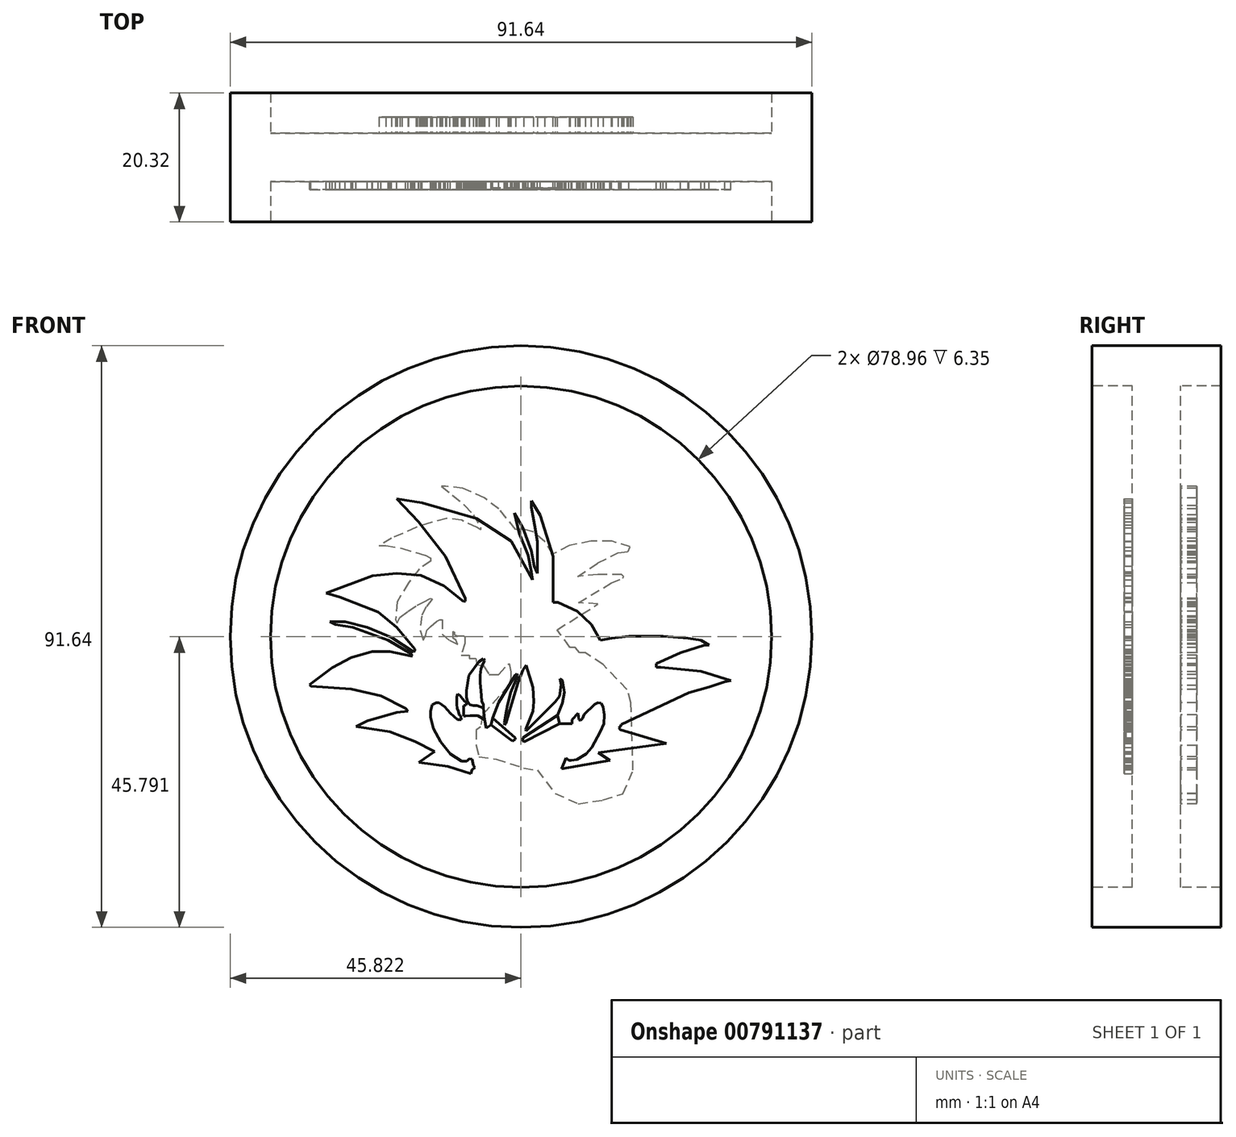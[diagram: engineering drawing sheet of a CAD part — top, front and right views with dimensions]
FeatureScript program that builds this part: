
annotation { "Feature Type Name" : "Feature", "Feature Type Description" : "" }
export const myFeature = defineFeature(function(context is Context, id is Id, definition is map)
    precondition{}
    {
        {
            var Q0;
            Q0=qCreatedBy(makeId("Front.planeOp"),FACE);
            var sketch = newSketch(context, id + "F0", { "sketchPlane" : qUnion([Q0])});
            skLineSegment(sketch, "E0", {"start": v(6.69, 2.2) * mm, "end": v(14.29, 3.57) * mm});
            skLineSegment(sketch, "E1", {"start": v(14.29, 3.57) * mm, "end": v(12.43, 4.77) * mm});
            skLineSegment(sketch, "E2", {"start": v(12.43, 4.77) * mm, "end": v(23.14, 6.2) * mm});
            skLineSegment(sketch, "E3", {"start": v(23.14, 6.2) * mm, "end": v(15.9, 8.36) * mm});
            skLineSegment(sketch, "E4", {"start": v(33.33, 16.13) * mm, "end": v(28.65, 17.57) * mm});
            skLineSegment(sketch, "E5", {"start": v(28.65, 17.57) * mm, "end": v(22.24, 18.23) * mm});
            skLineSegment(sketch, "E6", {"start": v(22.24, 18.23) * mm, "end": v(21.59, 18.23) * mm});
            skLineSegment(sketch, "E7", {"start": v(21.59, 18.23) * mm, "end": v(21.59, 18.77) * mm});
            skLineSegment(sketch, "E8", {"start": v(21.59, 18.77) * mm, "end": v(25.36, 20.5) * mm});
            skLineSegment(sketch, "E9", {"start": v(25.36, 20.5) * mm, "end": v(29.19, 21.7) * mm});
            skLineSegment(sketch, "E10", {"start": v(29.19, 21.7) * mm, "end": v(29.88, 21.7) * mm});
            skLineSegment(sketch, "E11", {"start": v(29.88, 21.7) * mm, "end": v(28.64, 22.43) * mm});
            skLineSegment(sketch, "E12", {"start": v(28.64, 22.43) * mm, "end": v(26.6, 22.76) * mm});
            skLineSegment(sketch, "E13", {"start": v(26.6, 22.76) * mm, "end": v(22.63, 23.11) * mm});
            skLineSegment(sketch, "E14", {"start": v(22.63, 23.11) * mm, "end": v(17.27, 23.11) * mm});
            skLineSegment(sketch, "E15", {"start": v(17.27, 23.11) * mm, "end": v(14.56, 22.79) * mm});
            skLineSegment(sketch, "E16", {"start": v(14.56, 22.79) * mm, "end": v(12.77, 22.49) * mm});
            skLineSegment(sketch, "E17", {"start": v(12.77, 22.49) * mm, "end": v(11.34, 24.94) * mm});
            skLineSegment(sketch, "E18", {"start": v(11.34, 24.94) * mm, "end": v(9.16, 27.06) * mm});
            skLineSegment(sketch, "E19", {"start": v(9.16, 27.06) * mm, "end": v(6.07, 28.46) * mm});
            skLineSegment(sketch, "E20", {"start": v(6.07, 28.46) * mm, "end": v(5.34, 28.46) * mm});
            skLineSegment(sketch, "E21", {"start": v(5.34, 28.46) * mm, "end": v(5.34, 35.65) * mm});
            skLineSegment(sketch, "E22", {"start": v(5.34, 35.65) * mm, "end": v(4.38, 38.73) * mm});
            skLineSegment(sketch, "E23", {"start": v(4.38, 38.73) * mm, "end": v(3.32, 42.13) * mm});
            skLineSegment(sketch, "E24", {"start": v(3.32, 42.13) * mm, "end": v(1.92, 44.45) * mm});
            skLineSegment(sketch, "E25", {"start": v(1.92, 44.45) * mm, "end": v(1.92, 43.43) * mm});
            skLineSegment(sketch, "E26", {"start": v(1.92, 43.43) * mm, "end": v(2.4, 40.62) * mm});
            skLineSegment(sketch, "E27", {"start": v(2.4, 40.62) * mm, "end": v(2.87, 38.04) * mm});
            skLineSegment(sketch, "E28", {"start": v(2.87, 38.04) * mm, "end": v(2.87, 33.02) * mm});
            skLineSegment(sketch, "E29", {"start": v(2.87, 33.02) * mm, "end": v(2.34, 34.15) * mm});
            skLineSegment(sketch, "E30", {"start": v(2.34, 34.15) * mm, "end": v(1.92, 36.55) * mm});
            skLineSegment(sketch, "E31", {"start": v(1.92, 36.55) * mm, "end": v(0.54, 40.2) * mm});
            skLineSegment(sketch, "E32", {"start": v(0.54, 40.2) * mm, "end": v(-0.78, 42.53) * mm});
            skLineSegment(sketch, "E33", {"start": v(-0.78, 42.53) * mm, "end": v(0, 39.3) * mm});
            skLineSegment(sketch, "E34", {"start": v(0, 39.3) * mm, "end": v(0.9, 37.15) * mm});
            skLineSegment(sketch, "E35", {"start": v(0.9, 37.15) * mm, "end": v(1.4, 35.88) * mm});
            skLineSegment(sketch, "E36", {"start": v(1.4, 35.88) * mm, "end": v(1.92, 33.27) * mm});
            skLineSegment(sketch, "E37", {"start": v(1.92, 33.27) * mm, "end": v(2.05, 31.99) * mm});
            skLineSegment(sketch, "E38", {"start": v(2.05, 31.99) * mm, "end": v(-1.3, 38.06) * mm});
            skLineSegment(sketch, "E39", {"start": v(-1.3, 38.06) * mm, "end": v(-6.74, 41.63) * mm});
            skLineSegment(sketch, "E40", {"start": v(-6.74, 41.63) * mm, "end": v(-15.3, 44.12) * mm});
            skLineSegment(sketch, "E41", {"start": v(-15.3, 44.12) * mm, "end": v(-19.32, 44.78) * mm});
            skLineSegment(sketch, "E42", {"start": v(-19.32, 44.78) * mm, "end": v(-15.9, 41.15) * mm});
            skLineSegment(sketch, "E43", {"start": v(-15.9, 41.15) * mm, "end": v(-11.62, 35.7) * mm});
            skLineSegment(sketch, "E44", {"start": v(-11.62, 35.7) * mm, "end": v(-8.53, 29.1) * mm});
            skLineSegment(sketch, "E45", {"start": v(-8.53, 29.1) * mm, "end": v(-8.53, 28.6) * mm});
            skLineSegment(sketch, "E46", {"start": v(-8.53, 28.6) * mm, "end": v(-8.77, 28.58) * mm});
            skLineSegment(sketch, "E47", {"start": v(-8.77, 28.58) * mm, "end": v(-11.9, 31.02) * mm});
            skLineSegment(sketch, "E48", {"start": v(-11.9, 31.02) * mm, "end": v(-15.5, 32.67) * mm});
            skLineSegment(sketch, "E49", {"start": v(-15.5, 32.67) * mm, "end": v(-19.32, 33.02) * mm});
            skLineSegment(sketch, "E50", {"start": v(-19.32, 33.02) * mm, "end": v(-23.1, 32.62) * mm});
            skLineSegment(sketch, "E51", {"start": v(-23.1, 32.62) * mm, "end": v(-30.42, 29.92) * mm});
            skLineSegment(sketch, "E52", {"start": v(-30.42, 29.92) * mm, "end": v(-28.29, 29.28) * mm});
            skLineSegment(sketch, "E53", {"start": v(-28.29, 29.28) * mm, "end": v(-22.24, 26.94) * mm});
            skLineSegment(sketch, "E54", {"start": v(-22.24, 26.94) * mm, "end": v(-19.32, 24.52) * mm});
            skLineSegment(sketch, "E55", {"start": v(-19.32, 24.52) * mm, "end": v(-16.47, 21.1) * mm});
            skLineSegment(sketch, "E56", {"start": v(-16.47, 21.1) * mm, "end": v(-16.47, 20.78) * mm});
            skLineSegment(sketch, "E57", {"start": v(-16.47, 20.78) * mm, "end": v(-16.65, 20.64) * mm});
            skLineSegment(sketch, "E58", {"start": v(-16.65, 20.64) * mm, "end": v(-20.12, 22.92) * mm});
            skLineSegment(sketch, "E59", {"start": v(-20.12, 22.92) * mm, "end": v(-23.94, 24.52) * mm});
            skLineSegment(sketch, "E60", {"start": v(-23.94, 24.52) * mm, "end": v(-27.47, 25.39) * mm});
            skLineSegment(sketch, "E61", {"start": v(-27.47, 25.39) * mm, "end": v(-29.83, 25.39) * mm});
            skLineSegment(sketch, "E62", {"start": v(-29.83, 25.39) * mm, "end": v(-29, 24.92) * mm});
            skLineSegment(sketch, "E63", {"start": v(-29, 24.92) * mm, "end": v(-26.27, 24.52) * mm});
            skLineSegment(sketch, "E64", {"start": v(-26.27, 24.52) * mm, "end": v(-20.64, 22.5) * mm});
            skLineSegment(sketch, "E65", {"start": v(-20.64, 22.5) * mm, "end": v(-17.1, 20.37) * mm});
            skLineSegment(sketch, "E66", {"start": v(-17.1, 20.37) * mm, "end": v(-16.81, 20.02) * mm});
            skLineSegment(sketch, "E67", {"start": v(-16.81, 20.02) * mm, "end": v(-17.1, 20.02) * mm});
            skLineSegment(sketch, "E68", {"start": v(-17.1, 20.02) * mm, "end": v(-20.39, 20.71) * mm});
            skLineSegment(sketch, "E69", {"start": v(-20.39, 20.71) * mm, "end": v(-23.2, 20.71) * mm});
            skLineSegment(sketch, "E70", {"start": v(-23.2, 20.71) * mm, "end": v(-26.48, 19.74) * mm});
            skLineSegment(sketch, "E71", {"start": v(-26.48, 19.74) * mm, "end": v(-29.49, 18.17) * mm});
            skLineSegment(sketch, "E72", {"start": v(-29.49, 18.17) * mm, "end": v(-33.04, 15.49) * mm});
            skLineSegment(sketch, "E73", {"start": v(-33.04, 15.49) * mm, "end": v(-32.85, 15.23) * mm});
            skLineSegment(sketch, "E74", {"start": v(-32.85, 15.23) * mm, "end": v(-26.48, 14.77) * mm});
            skLineSegment(sketch, "E75", {"start": v(-26.48, 14.77) * mm, "end": v(-21.8, 13.7) * mm});
            skLineSegment(sketch, "E76", {"start": v(-21.8, 13.7) * mm, "end": v(-17.92, 11.75) * mm});
            skLineSegment(sketch, "E77", {"start": v(-17.92, 11.75) * mm, "end": v(-17.56, 11.31) * mm});
            skLineSegment(sketch, "E78", {"start": v(-17.56, 11.31) * mm, "end": v(-19.32, 11.13) * mm});
            skLineSegment(sketch, "E79", {"start": v(-19.32, 11.13) * mm, "end": v(-23.93, 9.75) * mm});
            skLineSegment(sketch, "E80", {"start": v(-23.93, 9.75) * mm, "end": v(-25.75, 8.87) * mm});
            skLineSegment(sketch, "E81", {"start": v(-25.75, 8.87) * mm, "end": v(-20.4, 8.05) * mm});
            skLineSegment(sketch, "E82", {"start": v(-20.4, 8.05) * mm, "end": v(-16.47, 6.52) * mm});
            skLineSegment(sketch, "E83", {"start": v(-16.47, 6.52) * mm, "end": v(-13.33, 4.92) * mm});
            skLineSegment(sketch, "E84", {"start": v(-13.33, 4.92) * mm, "end": v(-15.85, 3.22) * mm});
            skLineSegment(sketch, "E85", {"start": v(-15.85, 3.22) * mm, "end": v(-11.27, 2.57) * mm});
            skLineSegment(sketch, "E86", {"start": v(-11.27, 2.57) * mm, "end": v(-7.62, 1.43) * mm});
            skLineSegment(sketch, "E87", {"start": v(-7.62, 1.43) * mm, "end": v(-7.42, 2.08) * mm});
            skLineSegment(sketch, "E88", {"start": v(-7.42, 2.08) * mm, "end": v(-6.99, 2.42) * mm});
            skLineSegment(sketch, "E89", {"start": v(-6.99, 2.42) * mm, "end": v(-7.26, 2.76) * mm});
            skLineSegment(sketch, "E90", {"start": v(-7.26, 2.76) * mm, "end": v(-7.45, 3.76) * mm});
            skLineSegment(sketch, "E91", {"start": v(-7.45, 3.76) * mm, "end": v(-7.87, 3.79) * mm});
            skLineSegment(sketch, "E92", {"start": v(-7.87, 3.79) * mm, "end": v(-8.25, 3.39) * mm});
            skLineSegment(sketch, "E93", {"start": v(-8.25, 3.39) * mm, "end": v(-9.1, 3.45) * mm});
            skLineSegment(sketch, "E94", {"start": v(-9.1, 3.45) * mm, "end": v(-10.85, 4.56) * mm});
            skLineSegment(sketch, "E95", {"start": v(-10.85, 4.56) * mm, "end": v(-12.41, 6.46) * mm});
            skLineSegment(sketch, "E96", {"start": v(-12.41, 6.46) * mm, "end": v(-13.57, 8.58) * mm});
            skLineSegment(sketch, "E97", {"start": v(-13.57, 8.58) * mm, "end": v(-14.01, 10.34) * mm});
            skLineSegment(sketch, "E98", {"start": v(-14.01, 10.34) * mm, "end": v(-14.01, 11.32) * mm});
            skLineSegment(sketch, "E99", {"start": v(-14.01, 11.32) * mm, "end": v(-13.71, 12.28) * mm});
            skLineSegment(sketch, "E100", {"start": v(-13.71, 12.28) * mm, "end": v(-13.07, 12.65) * mm});
            skLineSegment(sketch, "E101", {"start": v(-13.07, 12.65) * mm, "end": v(-12.65, 12.62) * mm});
            skLineSegment(sketch, "E102", {"start": v(-12.65, 12.62) * mm, "end": v(-11.74, 11.98) * mm});
            skLineSegment(sketch, "E103", {"start": v(-11.74, 11.98) * mm, "end": v(-10.88, 10.95) * mm});
            skLineSegment(sketch, "E104", {"start": v(-10.88, 10.95) * mm, "end": v(-9.74, 9.99) * mm});
            skLineSegment(sketch, "E105", {"start": v(-9.74, 9.99) * mm, "end": v(-9.17, 9.94) * mm});
            skLineSegment(sketch, "E106", {"start": v(-9.17, 9.94) * mm, "end": v(-9.23, 10.5) * mm});
            skLineSegment(sketch, "E107", {"start": v(-9.23, 10.5) * mm, "end": v(-9.48, 10.72) * mm});
            skLineSegment(sketch, "E108", {"start": v(-9.48, 10.72) * mm, "end": v(-9.58, 11.26) * mm});
            skLineSegment(sketch, "E109", {"start": v(-9.58, 11.26) * mm, "end": v(-9.77, 11.77) * mm});
            skLineSegment(sketch, "E110", {"start": v(-9.77, 11.77) * mm, "end": v(-9.87, 12.38) * mm});
            skLineSegment(sketch, "E111", {"start": v(-9.87, 12.38) * mm, "end": v(-9.87, 13.54) * mm});
            skLineSegment(sketch, "E112", {"start": v(-9.87, 13.54) * mm, "end": v(-9.74, 14.03) * mm});
            skLineSegment(sketch, "E113", {"start": v(-9.74, 14.03) * mm, "end": v(-9.38, 13.8) * mm});
            skLineSegment(sketch, "E114", {"start": v(-9.38, 13.8) * mm, "end": v(-8.94, 13.27) * mm});
            skLineSegment(sketch, "E115", {"start": v(-8.94, 13.27) * mm, "end": v(-8.56, 12.8) * mm});
            skLineSegment(sketch, "E116", {"start": v(-8.56, 12.8) * mm, "end": v(-8.38, 12.7) * mm});
            skLineSegment(sketch, "E117", {"start": v(-8.38, 12.7) * mm, "end": v(-8.35, 12.54) * mm});
            skLineSegment(sketch, "E118", {"start": v(-8.35, 12.54) * mm, "end": v(-8.38, 12.22) * mm});
            skLineSegment(sketch, "E119", {"start": v(-8.38, 12.22) * mm, "end": v(-8.78, 12.15) * mm});
            skLineSegment(sketch, "E120", {"start": v(-8.78, 12.15) * mm, "end": v(-8.78, 10.53) * mm});
            skLineSegment(sketch, "E121", {"start": v(-8.78, 10.53) * mm, "end": v(-8.43, 10.5) * mm});
            skLineSegment(sketch, "E122", {"start": v(-8.43, 10.5) * mm, "end": v(-7.78, 10.61) * mm});
            skLineSegment(sketch, "E123", {"start": v(-7.78, 10.61) * mm, "end": v(-7.1, 10.61) * mm});
            skLineSegment(sketch, "E124", {"start": v(-7.1, 10.61) * mm, "end": v(-6.58, 10.58) * mm});
            skLineSegment(sketch, "E125", {"start": v(-6.58, 10.58) * mm, "end": v(-5.45, 9.94) * mm});
            skLineSegment(sketch, "E126", {"start": v(-5.45, 9.94) * mm, "end": v(-5.23, 8.63) * mm});
            skLineSegment(sketch, "E127", {"start": v(-5.23, 8.63) * mm, "end": v(-4.43, 9.13) * mm});
            skLineSegment(sketch, "E128", {"start": v(-4.43, 9.13) * mm, "end": v(-1.1, 6.6) * mm});
            skLineSegment(sketch, "E129", {"start": v(-1.1, 6.6) * mm, "end": v(-0.65, 6.83) * mm});
            skLineSegment(sketch, "E130", {"start": v(-0.65, 6.83) * mm, "end": v(-0.65, 7.12) * mm});
            skLineSegment(sketch, "E131", {"start": v(-0.65, 7.12) * mm, "end": v(-2.15, 8.44) * mm});
            skLineSegment(sketch, "E132", {"start": v(-2.15, 8.44) * mm, "end": v(-4.2, 10.24) * mm});
            skLineSegment(sketch, "E133", {"start": v(-4.2, 10.24) * mm, "end": v(-3.22, 12.7) * mm});
            skLineSegment(sketch, "E134", {"start": v(-3.22, 12.7) * mm, "end": v(-0.65, 16.91) * mm});
            skLineSegment(sketch, "E135", {"start": v(-0.65, 16.91) * mm, "end": v(-0.42, 17.16) * mm});
            skLineSegment(sketch, "E136", {"start": v(-0.42, 17.16) * mm, "end": v(-0.27, 16.9) * mm});
            skLineSegment(sketch, "E137", {"start": v(-0.27, 16.9) * mm, "end": v(-1.36, 14.26) * mm});
            skLineSegment(sketch, "E138", {"start": v(-1.36, 14.26) * mm, "end": v(-1.85, 12.28) * mm});
            skLineSegment(sketch, "E139", {"start": v(-1.85, 12.28) * mm, "end": v(-2.07, 11.26) * mm});
            skLineSegment(sketch, "E140", {"start": v(-2.07, 11.26) * mm, "end": v(-2.35, 9.44) * mm});
            skLineSegment(sketch, "E141", {"start": v(-2.35, 9.44) * mm, "end": v(-2.3, 9.1) * mm});
            skLineSegment(sketch, "E142", {"start": v(-2.3, 9.1) * mm, "end": v(-2.08, 9.39) * mm});
            skLineSegment(sketch, "E143", {"start": v(-2.08, 9.39) * mm, "end": v(-1.23, 12.41) * mm});
            skLineSegment(sketch, "E144", {"start": v(-1.23, 12.41) * mm, "end": v(-0.23, 15.78) * mm});
            skLineSegment(sketch, "E145", {"start": v(-0.23, 15.78) * mm, "end": v(0.58, 17.74) * mm});
            skLineSegment(sketch, "E146", {"start": v(0.58, 17.74) * mm, "end": v(1.04, 18.55) * mm});
            skLineSegment(sketch, "E147", {"start": v(1.04, 18.55) * mm, "end": v(2.14, 15.06) * mm});
            skLineSegment(sketch, "E148", {"start": v(2.14, 15.06) * mm, "end": v(2.29, 12.82) * mm});
            skLineSegment(sketch, "E149", {"start": v(2.29, 12.82) * mm, "end": v(2.18, 11.26) * mm});
            skLineSegment(sketch, "E150", {"start": v(2.18, 11.26) * mm, "end": v(1.01, 8.44) * mm});
            skLineSegment(sketch, "E151", {"start": v(1.01, 8.44) * mm, "end": v(1.06, 8.18) * mm});
            skLineSegment(sketch, "E152", {"start": v(1.06, 8.18) * mm, "end": v(5.65, 12.78) * mm});
            skLineSegment(sketch, "E153", {"start": v(5.65, 12.78) * mm, "end": v(6.31, 13.64) * mm});
            skLineSegment(sketch, "E154", {"start": v(6.31, 13.64) * mm, "end": v(6.58, 15.47) * mm});
            skLineSegment(sketch, "E155", {"start": v(6.58, 15.47) * mm, "end": v(6.48, 16.03) * mm});
            skLineSegment(sketch, "E156", {"start": v(6.48, 16.03) * mm, "end": v(6.41, 16.44) * mm});
            skLineSegment(sketch, "E157", {"start": v(6.41, 16.44) * mm, "end": v(6.78, 16.17) * mm});
            skLineSegment(sketch, "E158", {"start": v(6.78, 16.17) * mm, "end": v(7.1, 14.26) * mm});
            skLineSegment(sketch, "E159", {"start": v(7.1, 14.26) * mm, "end": v(6.81, 12.58) * mm});
            skLineSegment(sketch, "E160", {"start": v(6.81, 12.58) * mm, "end": v(6.27, 11.26) * mm});
            skLineSegment(sketch, "E161", {"start": v(6.27, 11.26) * mm, "end": v(6.01, 10.65) * mm});
            skLineSegment(sketch, "E162", {"start": v(6.01, 10.65) * mm, "end": v(0.57, 7.12) * mm});
            skLineSegment(sketch, "E163", {"start": v(0.57, 7.12) * mm, "end": v(0.53, 6.6) * mm});
            skLineSegment(sketch, "E164", {"start": v(0.53, 6.6) * mm, "end": v(0.75, 6.44) * mm});
            skLineSegment(sketch, "E165", {"start": v(0.75, 6.44) * mm, "end": v(6.31, 9.34) * mm});
            skLineSegment(sketch, "E166", {"start": v(6.31, 9.34) * mm, "end": v(8.31, 9.34) * mm});
            skLineSegment(sketch, "E167", {"start": v(8.31, 9.34) * mm, "end": v(8.31, 9.94) * mm});
            skLineSegment(sketch, "E168", {"start": v(8.31, 9.94) * mm, "end": v(9.23, 11) * mm});
            skLineSegment(sketch, "E169", {"start": v(9.23, 11) * mm, "end": v(9.42, 9.94) * mm});
            skLineSegment(sketch, "E170", {"start": v(9.42, 9.94) * mm, "end": v(9.67, 9.84) * mm});
            skLineSegment(sketch, "E171", {"start": v(9.67, 9.84) * mm, "end": v(9.93, 10.14) * mm});
            skLineSegment(sketch, "E172", {"start": v(9.93, 10.14) * mm, "end": v(10.2, 10.8) * mm});
            skLineSegment(sketch, "E173", {"start": v(10.2, 10.8) * mm, "end": v(11.85, 12.35) * mm});
            skLineSegment(sketch, "E174", {"start": v(11.85, 12.35) * mm, "end": v(12.35, 12.62) * mm});
            skLineSegment(sketch, "E175", {"start": v(12.35, 12.62) * mm, "end": v(12.85, 12.59) * mm});
            skLineSegment(sketch, "E176", {"start": v(12.85, 12.59) * mm, "end": v(13.18, 11.99) * mm});
            skLineSegment(sketch, "E177", {"start": v(13.18, 11.99) * mm, "end": v(13.4, 10.7) * mm});
            skLineSegment(sketch, "E178", {"start": v(13.4, 10.7) * mm, "end": v(13.3, 9.34) * mm});
            skLineSegment(sketch, "E179", {"start": v(13.3, 9.34) * mm, "end": v(12.76, 8.03) * mm});
            skLineSegment(sketch, "E180", {"start": v(12.76, 8.03) * mm, "end": v(11.39, 5.6) * mm});
            skLineSegment(sketch, "E181", {"start": v(11.39, 5.6) * mm, "end": v(10.5, 4.59) * mm});
            skLineSegment(sketch, "E182", {"start": v(10.5, 4.59) * mm, "end": v(9.05, 3.67) * mm});
            skLineSegment(sketch, "E183", {"start": v(9.05, 3.67) * mm, "end": v(8.19, 3.52) * mm});
            skLineSegment(sketch, "E184", {"start": v(8.19, 3.52) * mm, "end": v(7.83, 3.55) * mm});
            skLineSegment(sketch, "E185", {"start": v(7.83, 3.55) * mm, "end": v(7.37, 3.95) * mm});
            skLineSegment(sketch, "E186", {"start": v(7.37, 3.95) * mm, "end": v(6.69, 2.2) * mm});
            skLineSegment(sketch, "E187", {"start": v(-8.35, 12.54) * mm, "end": v(-8.14, 12.72) * mm});
            skLineSegment(sketch, "E188", {"start": v(-8.14, 12.72) * mm, "end": v(-8.35, 13.45) * mm});
            skLineSegment(sketch, "E189", {"start": v(-8.35, 13.45) * mm, "end": v(-8.35, 14.5) * mm});
            skLineSegment(sketch, "E190", {"start": v(-8.35, 14.5) * mm, "end": v(-7.92, 16.94) * mm});
            skLineSegment(sketch, "E191", {"start": v(-7.92, 16.94) * mm, "end": v(-6.34, 19.07) * mm});
            skLineSegment(sketch, "E192", {"start": v(-6.34, 19.07) * mm, "end": v(-5.68, 19.54) * mm});
            skLineSegment(sketch, "E193", {"start": v(-5.68, 19.54) * mm, "end": v(-5.48, 19.25) * mm});
            skLineSegment(sketch, "E194", {"start": v(-5.48, 19.25) * mm, "end": v(-5.7, 18.8) * mm});
            skLineSegment(sketch, "E195", {"start": v(-5.7, 18.8) * mm, "end": v(-6.04, 17.94) * mm});
            skLineSegment(sketch, "E196", {"start": v(-6.04, 17.94) * mm, "end": v(-6.2, 16.96) * mm});
            skLineSegment(sketch, "E197", {"start": v(-6.2, 16.96) * mm, "end": v(-6.2, 15.75) * mm});
            skLineSegment(sketch, "E198", {"start": v(-6.2, 15.75) * mm, "end": v(-6.05, 14.5) * mm});
            skLineSegment(sketch, "E199", {"start": v(-6.05, 14.5) * mm, "end": v(-5.93, 12.85) * mm});
            skLineSegment(sketch, "E200", {"start": v(-5.93, 12.85) * mm, "end": v(-5.65, 12.3) * mm});
            skLineSegment(sketch, "E201", {"start": v(-5.65, 12.3) * mm, "end": v(-5.65, 11.82) * mm});
            skLineSegment(sketch, "E202", {"start": v(-5.65, 11.82) * mm, "end": v(-6.7, 12.15) * mm});
            skLineSegment(sketch, "E203", {"start": v(-6.7, 12.15) * mm, "end": v(-7.25, 12.15) * mm});
            skLineSegment(sketch, "E204", {"start": v(-7.25, 12.15) * mm, "end": v(-7.76, 12.3) * mm});
            skLineSegment(sketch, "E205", {"start": v(-7.76, 12.3) * mm, "end": v(-8.14, 12.72) * mm});
            skLineSegment(sketch, "E206", {"start": v(15.9, 8.36) * mm, "end": v(15.64, 8.7) * mm});
            skLineSegment(sketch, "E207", {"start": v(15.64, 8.7) * mm, "end": v(15.9, 8.9) * mm});
            skLineSegment(sketch, "E208", {"start": v(15.9, 8.9) * mm, "end": v(16.03, 9.21) * mm});
            skLineSegment(sketch, "E209", {"start": v(16.03, 9.21) * mm, "end": v(26.73, 14.22) * mm});
            skLineSegment(sketch, "E210", {"start": v(26.73, 14.22) * mm, "end": v(29.93, 15.11) * mm});
            skLineSegment(sketch, "E211", {"start": v(29.93, 15.11) * mm, "end": v(32.36, 15.92) * mm});
            skLineSegment(sketch, "E212", {"start": v(32.36, 15.92) * mm, "end": v(33.33, 16.13) * mm});
            skLineSegment(sketch, "E213", {"start": v(-5.65, 11.82) * mm, "end": v(-5.45, 9.94) * mm});
            skLineSegment(sketch, "E214", {"start": v(-4.2, 10.24) * mm, "end": v(-4.43, 9.13) * mm});
            skLineSegment(sketch, "E215", {"start": v(6.01, 10.65) * mm, "end": v(6.31, 9.34) * mm});
            skPoint(sketch, "E216", {"position": v(0.27, 23.02) * mm});
            skCircle(sketch, "E217", {"center": v(0.27, 23.02) * mm, "radius": 39.48 * mm});
            skCircle(sketch, "E218.0", {"center": v(0.27, 23.02) * mm, "radius": 45.83 * mm});
            skSolve(sketch);
        }
        {
            var Q0;
            Q0=makeQuery(id+"F0.imprint","IMPRINT",FACE,{"disambiguationData":[TD([[makeQuery(id+"F0.imprint","IMPRINT",EDGE,{"derivedFrom":sQuery(id+"F0.wireOp",EDGE,"E0")}),1.0]])]});
            extrude(context, id + "F1", {"entities" : qUnion([Q0]), "depth" : 5.08 * mm, "offsetDistance" : 25.4 * mm});
        }
        {
            var Q0;
            Q0=makeQuery(id+"F0.imprint","IMPRINT",FACE,{"disambiguationData":[TD([[makeQuery(id+"F0.imprint","IMPRINT",EDGE,{"derivedFrom":sQuery(id+"F0.wireOp",EDGE,"E128")}),1.0]])]});
            var Q1;
            Q1=makeQuery(id+"F0.imprint","IMPRINT",FACE,{"disambiguationData":[TD([[makeQuery(id+"F0.imprint","IMPRINT",EDGE,{"derivedFrom":sQuery(id+"F0.wireOp",EDGE,"E118")}),1.0]])]});
            extrude(context, id + "F2", {"entities" : qUnion([Q0, Q1]), "operationType" : NewBodyOperationType.ADD, "depth" : 4.83 * mm, "offsetDistance" : 25.4 * mm});
        }
        {
            var Q0;
            Q0=makeQuery(id+"F0.imprint","IMPRINT",FACE,{"disambiguationData":[TD([[makeQuery(id+"F0.imprint","IMPRINT",EDGE,{"derivedFrom":sQuery(id+"F0.wireOp",EDGE,"E162")}),1.0]])]});
            extrude(context, id + "F3", {"entities" : qUnion([Q0]), "operationType" : NewBodyOperationType.ADD, "depth" : 4.83 * mm, "offsetDistance" : 25.4 * mm});
        }
        {
            var Q0;
            Q0=makeQuery(id+"F0.imprint","IMPRINT",FACE,{"disambiguationData":[TD([[makeQuery(id+"F0.imprint","IMPRINT",EDGE,{"derivedFrom":sQuery(id+"F0.wireOp",EDGE,"E0")}),-1.0]])]});
            var Q1;
            Q1=makeQuery(id+"F0.imprint","IMPRINT",FACE,{"disambiguationData":[TD([[makeQuery(id+"F0.imprint","IMPRINT",EDGE,{"derivedFrom":sQuery(id+"F0.wireOp",EDGE,"E188")}),-1.0]])]});
            extrude(context, id + "F4", {"entities" : qUnion([Q0, Q1]), "depth" : 3.8 * mm, "offsetDistance" : 25.4 * mm});
        }
        {
            var Q0;
            Q0=makeQuery(id+"F0.imprint","IMPRINT",FACE,{"disambiguationData":[TD([[makeQuery(id+"F0.imprint","IMPRINT",EDGE,{"derivedFrom":sQuery(id+"F0.wireOp",EDGE,"E0")}),-1.0]])]});
            var sketch = newSketch(context, id + "F5", { "sketchPlane" : qUnion([Q0])});
            skLineSegment(sketch, "E219", {"start": v(5.28, 36.04) * mm, "end": v(4, 38.05) * mm});
            skLineSegment(sketch, "E220", {"start": v(4, 38.05) * mm, "end": v(2.2, 39.53) * mm});
            skLineSegment(sketch, "E221", {"start": v(2.2, 39.53) * mm, "end": v(0.71, 39.95) * mm});
            skLineSegment(sketch, "E222", {"start": v(0.71, 39.95) * mm, "end": v(-0.58, 39.95) * mm});
            skLineSegment(sketch, "E223", {"start": v(-0.58, 39.95) * mm, "end": v(-3.23, 43.17) * mm});
            skLineSegment(sketch, "E224", {"start": v(-3.23, 43.17) * mm, "end": v(-5.49, 44.88) * mm});
            skLineSegment(sketch, "E225", {"start": v(-5.49, 44.88) * mm, "end": v(-8.9, 46.38) * mm});
            skLineSegment(sketch, "E226", {"start": v(-8.9, 46.38) * mm, "end": v(-11.6, 46.74) * mm});
            skLineSegment(sketch, "E227", {"start": v(-11.6, 46.74) * mm, "end": v(-12.25, 46.74) * mm});
            skLineSegment(sketch, "E228", {"start": v(-12.25, 46.74) * mm, "end": v(-10.53, 45.34) * mm});
            skLineSegment(sketch, "E229", {"start": v(-10.53, 45.34) * mm, "end": v(-8.56, 43.7) * mm});
            skLineSegment(sketch, "E230", {"start": v(-8.56, 43.7) * mm, "end": v(-7.26, 42.2) * mm});
            skLineSegment(sketch, "E231", {"start": v(-7.26, 42.2) * mm, "end": v(-6.08, 40.23) * mm});
            skLineSegment(sketch, "E232", {"start": v(-6.08, 40.23) * mm, "end": v(-6.08, 39.87) * mm});
            skLineSegment(sketch, "E233", {"start": v(-6.08, 39.87) * mm, "end": v(-6.7, 40.23) * mm});
            skLineSegment(sketch, "E234", {"start": v(-6.7, 40.23) * mm, "end": v(-9.1, 41.36) * mm});
            skLineSegment(sketch, "E235", {"start": v(-9.1, 41.36) * mm, "end": v(-11.49, 41.67) * mm});
            skLineSegment(sketch, "E236", {"start": v(-11.49, 41.67) * mm, "end": v(-13.94, 41.02) * mm});
            skLineSegment(sketch, "E237", {"start": v(-13.94, 41.02) * mm, "end": v(-16.28, 40.23) * mm});
            skLineSegment(sketch, "E238", {"start": v(-16.28, 40.23) * mm, "end": v(-20.14, 38.51) * mm});
            skLineSegment(sketch, "E239", {"start": v(-20.14, 38.51) * mm, "end": v(-22.09, 37.36) * mm});
            skLineSegment(sketch, "E240", {"start": v(-22.09, 37.36) * mm, "end": v(-21.04, 37.36) * mm});
            skLineSegment(sketch, "E241", {"start": v(-21.04, 37.36) * mm, "end": v(-18.5, 36.96) * mm});
            skLineSegment(sketch, "E242", {"start": v(-18.5, 36.96) * mm, "end": v(-14.82, 35.84) * mm});
            skLineSegment(sketch, "E243", {"start": v(-14.82, 35.84) * mm, "end": v(-14, 35.44) * mm});
            skLineSegment(sketch, "E244", {"start": v(-14, 35.44) * mm, "end": v(-14, 34.94) * mm});
            skLineSegment(sketch, "E245", {"start": v(-14, 34.94) * mm, "end": v(-15.75, 33.72) * mm});
            skLineSegment(sketch, "E246", {"start": v(-15.75, 33.72) * mm, "end": v(-17.5, 31.5) * mm});
            skLineSegment(sketch, "E247", {"start": v(-17.5, 31.5) * mm, "end": v(-19.24, 28.5) * mm});
            skLineSegment(sketch, "E248", {"start": v(-19.24, 28.5) * mm, "end": v(-19.52, 25.72) * mm});
            skLineSegment(sketch, "E249", {"start": v(-19.52, 25.72) * mm, "end": v(-19.24, 25.18) * mm});
            skLineSegment(sketch, "E250", {"start": v(-19.24, 25.18) * mm, "end": v(-18.8, 26.1) * mm});
            skLineSegment(sketch, "E251", {"start": v(-18.8, 26.1) * mm, "end": v(-17.52, 27.04) * mm});
            skLineSegment(sketch, "E252", {"start": v(-17.52, 27.04) * mm, "end": v(-16.08, 28) * mm});
            skLineSegment(sketch, "E253", {"start": v(-16.08, 28) * mm, "end": v(-15.04, 28.5) * mm});
            skLineSegment(sketch, "E254", {"start": v(-15.04, 28.5) * mm, "end": v(-14, 29.1) * mm});
            skLineSegment(sketch, "E255", {"start": v(-14, 29.1) * mm, "end": v(-13.72, 28.97) * mm});
            skLineSegment(sketch, "E256", {"start": v(-13.72, 28.97) * mm, "end": v(-14.7, 27.72) * mm});
            skLineSegment(sketch, "E257", {"start": v(-14.7, 27.72) * mm, "end": v(-15.4, 26.28) * mm});
            skLineSegment(sketch, "E258", {"start": v(-15.4, 26.28) * mm, "end": v(-15.6, 24.08) * mm});
            skLineSegment(sketch, "E259", {"start": v(-15.6, 24.08) * mm, "end": v(-15.15, 22.45) * mm});
            skLineSegment(sketch, "E260", {"start": v(-15.15, 22.45) * mm, "end": v(-14.75, 23.29) * mm});
            skLineSegment(sketch, "E261", {"start": v(-14.75, 23.29) * mm, "end": v(-14.57, 24.08) * mm});
            skLineSegment(sketch, "E262", {"start": v(-14.57, 24.08) * mm, "end": v(-14, 24.64) * mm});
            skLineSegment(sketch, "E263", {"start": v(-14, 24.64) * mm, "end": v(-13.06, 25.46) * mm});
            skLineSegment(sketch, "E264", {"start": v(-13.06, 25.46) * mm, "end": v(-12.5, 25.72) * mm});
            skLineSegment(sketch, "E265", {"start": v(-12.5, 25.72) * mm, "end": v(-12.15, 25.72) * mm});
            skLineSegment(sketch, "E266", {"start": v(-12.15, 25.72) * mm, "end": v(-12.15, 24.64) * mm});
            skLineSegment(sketch, "E267", {"start": v(-12.15, 24.64) * mm, "end": v(-12.15, 23.45) * mm});
            skLineSegment(sketch, "E268", {"start": v(-12.15, 23.45) * mm, "end": v(-11.03, 22.45) * mm});
            skLineSegment(sketch, "E269", {"start": v(-11.03, 22.45) * mm, "end": v(-10, 21.96) * mm});
            skLineSegment(sketch, "E270", {"start": v(-10, 21.96) * mm, "end": v(-9.72, 21.82) * mm});
            skLineSegment(sketch, "E271", {"start": v(-9.72, 21.82) * mm, "end": v(-10, 22.45) * mm});
            skLineSegment(sketch, "E272", {"start": v(-10, 22.45) * mm, "end": v(-10.4, 22.8) * mm});
            skLineSegment(sketch, "E273", {"start": v(-10.4, 22.8) * mm, "end": v(-10.4, 23.67) * mm});
            skLineSegment(sketch, "E274", {"start": v(-10.4, 23.67) * mm, "end": v(-10.4, 23.83) * mm});
            skLineSegment(sketch, "E275", {"start": v(-10.4, 23.83) * mm, "end": v(-10.21, 23.74) * mm});
            skLineSegment(sketch, "E276", {"start": v(-10.21, 23.74) * mm, "end": v(-10.21, 23.35) * mm});
            skLineSegment(sketch, "E277", {"start": v(-10.21, 23.35) * mm, "end": v(-9.82, 23.16) * mm});
            skLineSegment(sketch, "E278", {"start": v(-9.82, 23.16) * mm, "end": v(-8.75, 23.16) * mm});
            skLineSegment(sketch, "E279", {"start": v(-8.75, 23.16) * mm, "end": v(-8.56, 22.99) * mm});
            skLineSegment(sketch, "E280", {"start": v(-8.56, 22.99) * mm, "end": v(-8.56, 21.96) * mm});
            skLineSegment(sketch, "E281", {"start": v(-8.56, 21.96) * mm, "end": v(-9.14, 20.15) * mm});
            skLineSegment(sketch, "E282", {"start": v(-9.14, 20.15) * mm, "end": v(-7.86, 20.15) * mm});
            skLineSegment(sketch, "E283", {"start": v(-7.86, 20.15) * mm, "end": v(-7.86, 19.6) * mm});
            skLineSegment(sketch, "E284", {"start": v(-7.86, 19.6) * mm, "end": v(-6.87, 19.6) * mm});
            skLineSegment(sketch, "E285", {"start": v(-6.87, 19.6) * mm, "end": v(-6.69, 18.65) * mm});
            skLineSegment(sketch, "E286", {"start": v(-6.69, 18.65) * mm, "end": v(-5.92, 18.45) * mm});
            skLineSegment(sketch, "E287", {"start": v(-5.92, 18.45) * mm, "end": v(-5.67, 18.45) * mm});
            skLineSegment(sketch, "E288", {"start": v(-5.67, 18.45) * mm, "end": v(-4.76, 17.06) * mm});
            skLineSegment(sketch, "E289", {"start": v(-4.76, 17.06) * mm, "end": v(-3.22, 17.06) * mm});
            skLineSegment(sketch, "E290", {"start": v(-3.22, 17.06) * mm, "end": v(-1.81, 18.65) * mm});
            skLineSegment(sketch, "E291", {"start": v(-1.81, 18.65) * mm, "end": v(-1.62, 18.8) * mm});
            skLineSegment(sketch, "E292", {"start": v(-1.62, 18.8) * mm, "end": v(-1.34, 17.5) * mm});
            skLineSegment(sketch, "E293", {"start": v(-1.34, 17.5) * mm, "end": v(-1.34, 16.45) * mm});
            skLineSegment(sketch, "E294", {"start": v(-1.34, 16.45) * mm, "end": v(-1.65, 15.33) * mm});
            skLineSegment(sketch, "E295", {"start": v(-1.65, 15.33) * mm, "end": v(-5.82, 10.69) * mm});
            skLineSegment(sketch, "E296", {"start": v(-5.82, 10.69) * mm, "end": v(-6.1, 8.8) * mm});
            skLineSegment(sketch, "E297", {"start": v(-6.1, 8.8) * mm, "end": v(-6.8, 8.34) * mm});
            skLineSegment(sketch, "E298", {"start": v(-6.8, 8.34) * mm, "end": v(-6.8, 5.87) * mm});
            skLineSegment(sketch, "E299", {"start": v(-6.8, 5.87) * mm, "end": v(-6.37, 4.1) * mm});
            skLineSegment(sketch, "E300", {"start": v(-6.37, 4.1) * mm, "end": v(-3.64, 3.75) * mm});
            skLineSegment(sketch, "E301", {"start": v(-3.64, 3.75) * mm, "end": v(0.67, 2.33) * mm});
            skLineSegment(sketch, "E302", {"start": v(0.67, 2.33) * mm, "end": v(2.85, 2.01) * mm});
            skLineSegment(sketch, "E303", {"start": v(2.85, 2.01) * mm, "end": v(5.63, -1.64) * mm});
            skLineSegment(sketch, "E304", {"start": v(5.63, -1.64) * mm, "end": v(9.28, -3.29) * mm});
            skLineSegment(sketch, "E305", {"start": v(9.28, -3.29) * mm, "end": v(13.22, -2.7) * mm});
            skLineSegment(sketch, "E306", {"start": v(13.22, -2.7) * mm, "end": v(16.33, -1.7) * mm});
            skLineSegment(sketch, "E307", {"start": v(16.33, -1.7) * mm, "end": v(17.92, 2) * mm});
            skLineSegment(sketch, "E308", {"start": v(17.92, 2) * mm, "end": v(17.6, 12.63) * mm});
            skLineSegment(sketch, "E309", {"start": v(17.6, 12.63) * mm, "end": v(16.97, 14.74) * mm});
            skLineSegment(sketch, "E310", {"start": v(16.97, 14.74) * mm, "end": v(13.17, 18.65) * mm});
            skLineSegment(sketch, "E311", {"start": v(13.17, 18.65) * mm, "end": v(10.37, 20.47) * mm});
            skLineSegment(sketch, "E312", {"start": v(10.37, 20.47) * mm, "end": v(9.48, 20.47) * mm});
            skLineSegment(sketch, "E313", {"start": v(9.48, 20.47) * mm, "end": v(8.8, 21.35) * mm});
            skLineSegment(sketch, "E314", {"start": v(8.8, 21.35) * mm, "end": v(7.96, 21.35) * mm});
            skLineSegment(sketch, "E315", {"start": v(7.96, 21.35) * mm, "end": v(5.98, 24.11) * mm});
            skLineSegment(sketch, "E316", {"start": v(5.98, 24.11) * mm, "end": v(12.38, 28.17) * mm});
            skLineSegment(sketch, "E317", {"start": v(12.38, 28.17) * mm, "end": v(9.3, 28.4) * mm});
            skLineSegment(sketch, "E318", {"start": v(9.3, 28.4) * mm, "end": v(14.5, 31.47) * mm});
            skLineSegment(sketch, "E319", {"start": v(14.5, 31.47) * mm, "end": v(16.33, 32.26) * mm});
            skLineSegment(sketch, "E320", {"start": v(16.33, 32.26) * mm, "end": v(16.44, 32.52) * mm});
            skLineSegment(sketch, "E321", {"start": v(16.44, 32.52) * mm, "end": v(16.13, 32.82) * mm});
            skLineSegment(sketch, "E322", {"start": v(16.13, 32.82) * mm, "end": v(12.36, 32.82) * mm});
            skLineSegment(sketch, "E323", {"start": v(12.36, 32.82) * mm, "end": v(9.57, 32.55) * mm});
            skLineSegment(sketch, "E324", {"start": v(9.57, 32.55) * mm, "end": v(9.16, 32.5) * mm});
            skLineSegment(sketch, "E325", {"start": v(9.16, 32.5) * mm, "end": v(12.36, 34.65) * mm});
            skLineSegment(sketch, "E326", {"start": v(12.36, 34.65) * mm, "end": v(15.56, 36.26) * mm});
            skLineSegment(sketch, "E327", {"start": v(15.56, 36.26) * mm, "end": v(17.1, 36.41) * mm});
            skLineSegment(sketch, "E328", {"start": v(17.1, 36.41) * mm, "end": v(17.47, 37.18) * mm});
            skLineSegment(sketch, "E329", {"start": v(17.47, 37.18) * mm, "end": v(14.57, 38.07) * mm});
            skLineSegment(sketch, "E330", {"start": v(14.57, 38.07) * mm, "end": v(11.3, 38.07) * mm});
            skLineSegment(sketch, "E331", {"start": v(11.3, 38.07) * mm, "end": v(7.84, 37.38) * mm});
            skLineSegment(sketch, "E332", {"start": v(7.84, 37.38) * mm, "end": v(5.28, 36.04) * mm});
            skCircle(sketch, "E333.0", {"center": v(0.27, 23.05) * mm, "radius": 45.82 * mm});
            skSolve(sketch);
        }
        {
            var Q0;
            Q0=makeQuery(id+"F5.imprint","IMPRINT",FACE,{"disambiguationData":[TD([[makeQuery(id+"F5.imprint","IMPRINT",EDGE,{"derivedFrom":sQuery(id+"F5.wireOp",EDGE,"E333.0")}),1.0]])]});
            extrude(context, id + "F6", {"entities" : qUnion([Q0]), "oppositeDirection" : true, "depth" : 10.16 * mm, "offsetDistance" : 25.4 * mm});
        }
        {
            var Q0;
            {var subQ36=sQuery(id+"F5.wireOp",EDGE,"E221");Q0=makeQuery(id+"F5.imprint","IMPRINT",FACE,{"disambiguationData":[TD([[makeQuery(id+"F5.imprint","IMPRINT",EDGE,{"derivedFrom":subQ36}),-1.0]])]});}
            var Q1;
            {var subQ5=sQuery(id+"F5.wireOp",EDGE,"E247");Q1=makeQuery(id+"F5.imprint","IMPRINT",FACE,{"disambiguationData":[TD([[makeQuery(id+"F5.imprint","IMPRINT",EDGE,{"derivedFrom":subQ5}),-1.0]])]});}
            var Q2;
            {var subQ0=sQuery(id+"F5.wireOp",EDGE,"E309");Q2=makeQuery(id+"F5.imprint","IMPRINT",FACE,{"disambiguationData":[TD([[makeQuery(id+"F5.imprint","IMPRINT",EDGE,{"derivedFrom":subQ0}),-1.0]])]});}
            var Q3;
            {var subQ4=sQuery(id+"F5.wireOp",EDGE,"E232");Q3=makeQuery(id+"F5.imprint","IMPRINT",FACE,{"disambiguationData":[TD([[makeQuery(id+"F5.imprint","IMPRINT",EDGE,{"derivedFrom":subQ4}),-1.0]])]});}
            var Q4;
            {var subQ0=makeQuery(id+"F0.imprint","IMPRINT",EDGE,{"derivedFrom":sQuery(id+"F0.wireOp",EDGE,"E23")});Q4=makeQuery(id+"F5.imprint","IMPRINT",FACE,{"disambiguationData":[TD([[makeQuery(id+"F5.imprint","IMPRINT",EDGE,{"derivedFrom":subQ0}),1.0]])]});}
            var Q5;
            {var subQ5=makeQuery(id+"F0.imprint","IMPRINT",EDGE,{"derivedFrom":sQuery(id+"F0.wireOp",EDGE,"E32")});Q5=makeQuery(id+"F5.imprint","IMPRINT",FACE,{"disambiguationData":[TD([[makeQuery(id+"F5.imprint","IMPRINT",EDGE,{"derivedFrom":subQ5}),1.0]])]});}
            var Q6;
            {var subQ0=sQuery(id+"F5.wireOp",EDGE,"E308");var subQ1=makeQuery(id+"F0.imprint","IMPRINT",EDGE,{"derivedFrom":sQuery(id+"F0.wireOp",EDGE,"E2")});var subQ2=makeQuery(id+"F5.imprint","INTERSECT",VERTEX,{"derivedFrom":[subQ1,subQ0]});Q6=makeQuery(id+"F5.imprint","IMPRINT",FACE,{"disambiguationData":[TD([[makeQuery(id+"F5.imprint","IMPRINT",EDGE,{"disambiguationData":[TD([[subQ2,-1.0]])],"derivedFrom":subQ0}),-1.0]])]});}
            extrude(context, id + "F7", {"entities" : qUnion([Q0, Q1, Q2, Q3, Q4, Q5, Q6]), "oppositeDirection" : true, "depth" : 3.8 * mm, "offsetDistance" : 25.4 * mm});
        }
        {
            var Q0;
            {var subQ9=sQuery(id+"F5.wireOp",EDGE,"E238");Q0=makeQuery(id+"F5.imprint","IMPRINT",FACE,{"disambiguationData":[TD([[makeQuery(id+"F5.imprint","IMPRINT",EDGE,{"derivedFrom":subQ9}),1.0]])]});}
            var Q1;
            {var subQ4=sQuery(id+"F5.wireOp",EDGE,"E223");Q1=makeQuery(id+"F5.imprint","IMPRINT",FACE,{"disambiguationData":[TD([[makeQuery(id+"F5.imprint","IMPRINT",EDGE,{"derivedFrom":subQ4}),1.0]])]});}
            var Q2;
            {var subQ24=sQuery(id+"F5.wireOp",EDGE,"E232");Q2=makeQuery(id+"F5.imprint","IMPRINT",FACE,{"disambiguationData":[TD([[makeQuery(id+"F5.imprint","IMPRINT",EDGE,{"derivedFrom":subQ24}),1.0]])]});}
            var Q3;
            {var subQ6=sQuery(id+"F5.wireOp",EDGE,"E317");Q3=makeQuery(id+"F5.imprint","IMPRINT",FACE,{"disambiguationData":[TD([[makeQuery(id+"F5.imprint","IMPRINT",EDGE,{"derivedFrom":subQ6}),1.0]])]});}
            var Q4;
            {var subQ0=sQuery(id+"F5.wireOp",EDGE,"E297");Q4=makeQuery(id+"F5.imprint","IMPRINT",FACE,{"disambiguationData":[TD([[makeQuery(id+"F5.imprint","IMPRINT",EDGE,{"derivedFrom":subQ0}),1.0]])]});}
            var Q5;
            {var subQ2=sQuery(id+"F5.wireOp",EDGE,"E221");Q5=makeQuery(id+"F5.imprint","IMPRINT",FACE,{"disambiguationData":[TD([[makeQuery(id+"F5.imprint","IMPRINT",EDGE,{"derivedFrom":subQ2}),1.0]])]});}
            var Q6;
            {var subQ1=makeQuery(id+"F0.imprint","IMPRINT",EDGE,{"derivedFrom":sQuery(id+"F0.wireOp",EDGE,"E206")});Q6=makeQuery(id+"F5.imprint","IMPRINT",FACE,{"disambiguationData":[TD([[makeQuery(id+"F5.imprint","IMPRINT",EDGE,{"derivedFrom":subQ1}),-1.0]])]});}
            extrude(context, id + "F8", {"entities" : qUnion([Q0, Q1, Q2, Q3, Q4, Q5, Q6]), "operationType" : NewBodyOperationType.ADD, "oppositeDirection" : true, "depth" : 6.35 * mm, "offsetDistance" : 25.4 * mm});
        }
        {
            var Q0;
            Q0=makeQuery(id+"F6.opExtrude","CAP_FACE",FACE,{"disambiguationData":[OSD([sQuery(id+"F0.wireOp",EDGE,"E217"),sQuery(id+"F5.wireOp",EDGE,"Urh2WCef-Zvhs-JE87-yzrO-q2sPZOutLoFk"),sQuery(id+"F5.wireOp",EDGE,"E333.0")])],"isStart":true});
            extrude(context, id + "F9", {"entities" : qUnion([Q0]), "operationType" : NewBodyOperationType.ADD, "depth" : 10.16 * mm, "offsetDistance" : 25.4 * mm});
        }
    });
